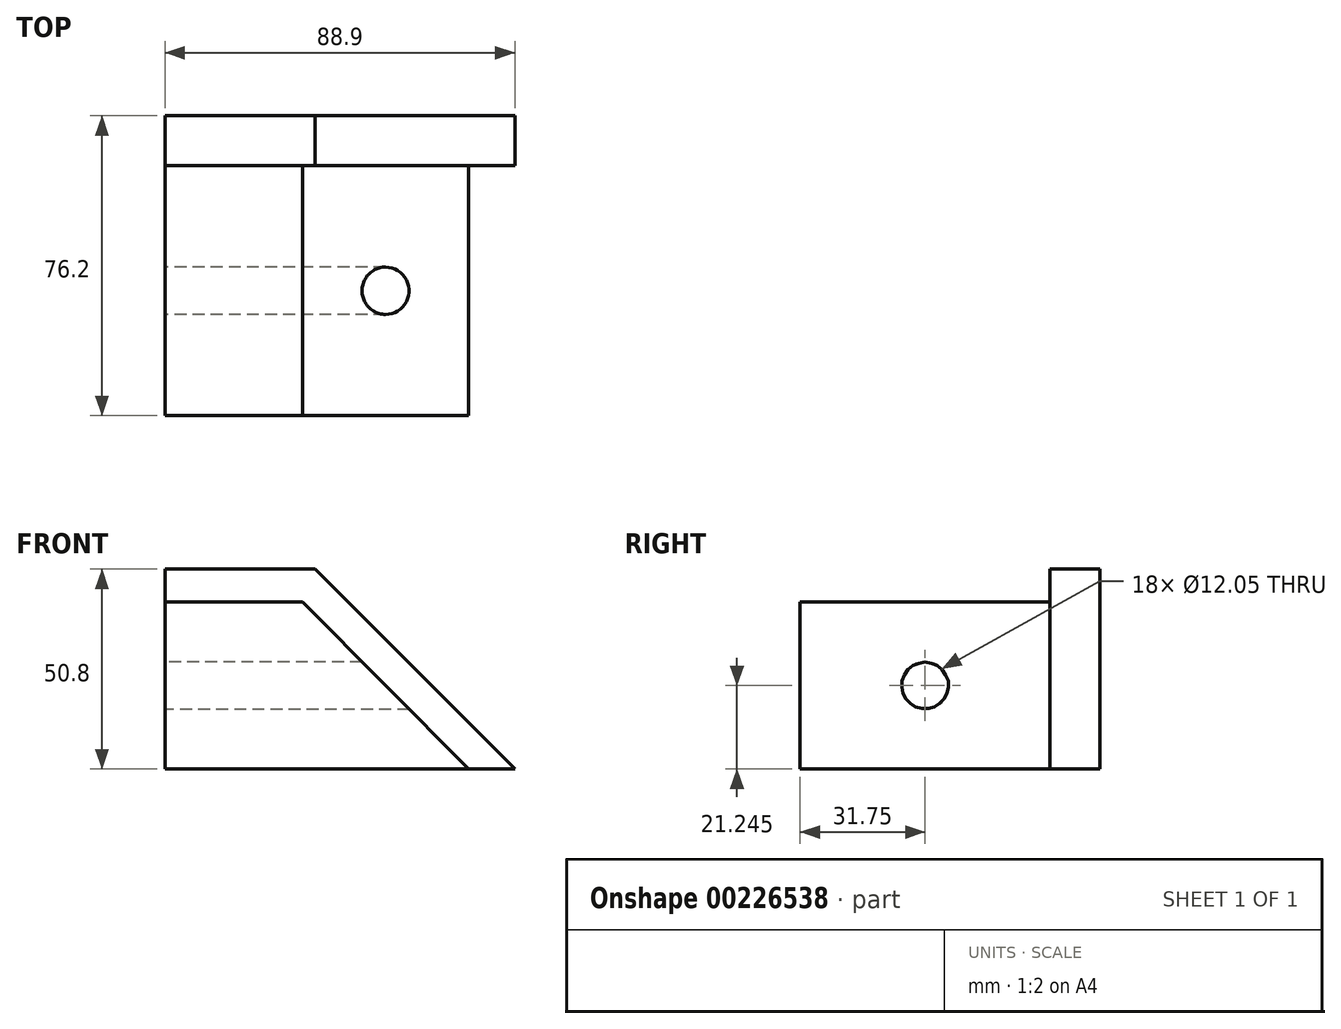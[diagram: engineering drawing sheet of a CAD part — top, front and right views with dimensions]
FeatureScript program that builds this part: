
annotation { "Feature Type Name" : "Feature", "Feature Type Description" : "" }
export const myFeature = defineFeature(function(context is Context, id is Id, definition is map)
    precondition{}
    {
        {
            var Q0;
            Q0=qCreatedBy(makeId("Front.planeOp"),FACE);
            var sketch = newSketch(context, id + "F0", { "sketchPlane" : qUnion([Q0])});
            skLineSegment(sketch, "E0", {"start": v(-38.1, 28.42) * mm, "end": v(0, 28.42) * mm});
            skLineSegment(sketch, "E1", {"start": v(0, 28.42) * mm, "end": v(50.8, -22.38) * mm});
            skLineSegment(sketch, "E2", {"start": v(-38.1, 28.42) * mm, "end": v(-38.1, -22.38) * mm});
            skLineSegment(sketch, "E3", {"start": v(-38.1, -22.38) * mm, "end": v(50.8, -22.38) * mm});
            skSolve(sketch);
        }
        {
            var Q0;
            Q0=makeQuery(id+"F0.imprint","IMPRINT",FACE,{"disambiguationData":[TD([[makeQuery(id+"F0.imprint","IMPRINT",EDGE,{"derivedFrom":sQuery(id+"F0.wireOp",EDGE,"E0")}),-1.0]])]});
            extrude(context, id + "F1", {"entities" : qUnion([Q0]), "depth" : 76.2 * mm});
        }
        {
            var Q0;
            Q0=makeQuery(id+"F1.opExtrude","CAP_FACE",FACE,{"disambiguationData":[OSD([sQuery(id+"F0.wireOp",EDGE,"E0"),sQuery(id+"F0.wireOp",EDGE,"E1"),sQuery(id+"F0.wireOp",EDGE,"E2"),sQuery(id+"F0.wireOp",EDGE,"E3")])],"isStart":false});
            var sketch = newSketch(context, id + "F2", { "sketchPlane" : qUnion([Q0])});
            skLineSegment(sketch, "E4", {"start": v(-38.1, 20.1) * mm, "end": v(-3.14, 20.1) * mm});
            skLineSegment(sketch, "E5", {"start": v(-3.14, 20.1) * mm, "end": v(39.08, -22.38) * mm});
            skLineSegment(sketch, "E6", {"start": v(-38.1, 20.1) * mm, "end": v(-38.1, 28.42) * mm});
            skLineSegment(sketch, "E7", {"start": v(-38.1, 28.42) * mm, "end": v(0, 28.42) * mm});
            skLineSegment(sketch, "E8", {"start": v(0, 28.42) * mm, "end": v(50.8, -22.38) * mm});
            skLineSegment(sketch, "E9", {"start": v(39.08, -22.38) * mm, "end": v(50.8, -22.38) * mm});
            skSolve(sketch);
        }
        {
            var Q0;
            Q0=makeQuery(id+"F2.imprint","IMPRINT",FACE,{"disambiguationData":[TD([[makeQuery(id+"F2.imprint","IMPRINT",EDGE,{"derivedFrom":sQuery(id+"F2.wireOp",EDGE,"E4")}),1.0]])]});
            extrude(context, id + "F3", {"entities" : qUnion([Q0]), "operationType" : NewBodyOperationType.REMOVE, "oppositeDirection" : true, "depth" : 63.5 * mm});
        }
        {
            var Q0;
            Q0=makeQuery(id+"F1.opExtrude","SWEPT_FACE",FACE,{"disambiguationData":[OSD([sQuery(id+"F0.wireOp",EDGE,"E2")])]});
            var sketch = newSketch(context, id + "F4", { "sketchPlane" : qUnion([Q0])});
            skLineSegment(sketch, "E10", {"start": v(44.45, 0) * mm, "end": v(44.45, -1.13) * mm});
            skCircle(sketch, "E11", {"center": v(44.45, -1.13) * mm, "radius": 6.03 * mm});
            skPoint(sketch, "E12.orphan", {"position": v(44.45, 20.1) * mm});
            skPoint(sketch, "E13.orphan", {"position": v(76.2, 0) * mm});
            skPoint(sketch, "E14.trimOffspring.end.orphan", {"position": v(44.45, -22.38) * mm});
            skSolve(sketch);
        }
        {
            var Q0;
            Q0 = qSketchRegion(id + "F4", true);
            extrude(context, id + "F5", {"entities" : qUnion([Q0]), "operationType" : NewBodyOperationType.REMOVE, "oppositeDirection" : true, "depth" : 254 * mm});
        }
    });
